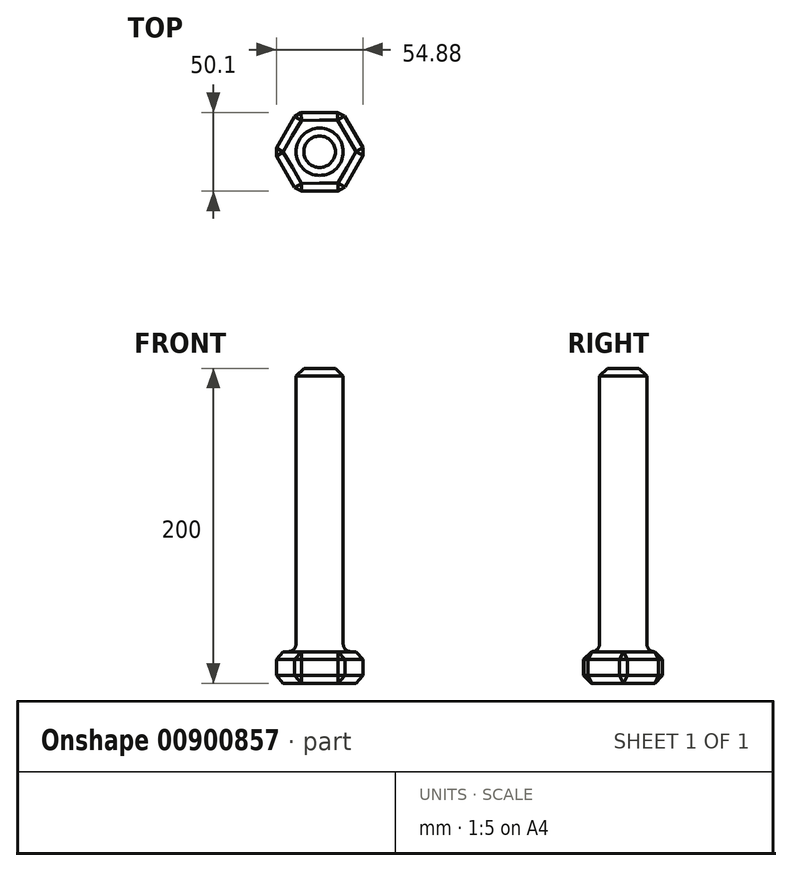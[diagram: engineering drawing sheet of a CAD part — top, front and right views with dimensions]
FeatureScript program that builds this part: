
annotation { "Feature Type Name" : "Feature", "Feature Type Description" : "" }
export const myFeature = defineFeature(function(context is Context, id is Id, definition is map)
    precondition{}
    {
        {
            var Q0;
            Q0=qCreatedBy(makeId("Top.planeOp"),FACE);
            var sketch = newSketch(context, id + "F0", { "sketchPlane" : qUnion([Q0])});
            skCircle(sketch, "E0.cCircle", {"center": v(0, 0) * mm, "radius": 25 * mm, "construction": true});
            skLineSegment(sketch, "E0.0", {"start": v(-28.87, -0.13) * mm, "end": v(-14.55, 24.94) * mm});
            skLineSegment(sketch, "E0.1", {"start": v(-14.55, 24.94) * mm, "end": v(14.32, 25.06) * mm});
            skLineSegment(sketch, "E0.2", {"start": v(14.32, 25.06) * mm, "end": v(28.87, 0.13) * mm});
            skLineSegment(sketch, "E0.3", {"start": v(28.87, 0.13) * mm, "end": v(14.55, -24.94) * mm});
            skLineSegment(sketch, "E0.4", {"start": v(14.55, -24.94) * mm, "end": v(-14.32, -25.06) * mm});
            skLineSegment(sketch, "E0.5", {"start": v(-14.32, -25.06) * mm, "end": v(-28.87, -0.13) * mm});
            skPoint(sketch, "E0.0.midPoint", {"position": v(-21.7, 12.4) * mm});
            skSolve(sketch);
        }
        {
            var Q0;
            Q0=makeQuery(id+"F0.imprint","IMPRINT",FACE,{"disambiguationData":[TD([[makeQuery(id+"F0.imprint","IMPRINT",EDGE,{"derivedFrom":sQuery(id+"F0.wireOp",EDGE,"E0.0")}),-1.0]])]});
            extrude(context, id + "F1", {"entities" : qUnion([Q0]), "depth" : 20 * mm, "offsetDistance" : 25 * mm});
        }
        {
            var Q0;
            Q0=qCreatedBy(makeId("Top.planeOp"),FACE);
            var sketch = newSketch(context, id + "F2", { "sketchPlane" : qUnion([Q0])});
            skCircle(sketch, "E1", {"center": v(0, 0) * mm, "radius": 15 * mm});
            skSolve(sketch);
        }
        {
            var Q0;
            Q0=makeQuery(id+"F2.imprint","IMPRINT",FACE,{"disambiguationData":[TD([[makeQuery(id+"F2.imprint","IMPRINT",EDGE,{"derivedFrom":sQuery(id+"F2.wireOp",EDGE,"E1")}),1.0]])]});
            extrude(context, id + "F3", {"entities" : qUnion([Q0]), "operationType" : NewBodyOperationType.ADD, "depth" : 200 * mm, "offsetDistance" : 25 * mm});
        }
        {
            var Q0;
            Q0=makeQuery(id+"F3.opExtrude","CAP_EDGE",EDGE,{"disambiguationData":[OSD([sQuery(id+"F2.wireOp",EDGE,"E1")])],"isStart":false});
            var Q1;
            Q1=makeQuery(id+"F1.opExtrude","CAP_EDGE",EDGE,{"disambiguationData":[OSD([sQuery(id+"F0.wireOp",EDGE,"E0.0")])],"isStart":false});
            var Q2;
            Q2=makeQuery(id+"F1.opExtrude","CAP_EDGE",EDGE,{"disambiguationData":[OSD([sQuery(id+"F0.wireOp",EDGE,"E0.5")])],"isStart":false});
            var Q3;
            Q3=makeQuery(id+"F1.opExtrude","CAP_EDGE",EDGE,{"disambiguationData":[OSD([sQuery(id+"F0.wireOp",EDGE,"E0.4")])],"isStart":false});
            var Q4;
            Q4=makeQuery(id+"F1.opExtrude","CAP_EDGE",EDGE,{"disambiguationData":[OSD([sQuery(id+"F0.wireOp",EDGE,"E0.3")])],"isStart":false});
            var Q5;
            Q5=makeQuery(id+"F1.opExtrude","CAP_EDGE",EDGE,{"disambiguationData":[OSD([sQuery(id+"F0.wireOp",EDGE,"E0.1")])],"isStart":false});
            var Q6;
            Q6=makeQuery(id+"F1.opExtrude","CAP_EDGE",EDGE,{"disambiguationData":[OSD([sQuery(id+"F0.wireOp",EDGE,"E0.2")])],"isStart":false});
            var Q7;
            Q7=makeQuery(id+"F1.opExtrude","CAP_EDGE",EDGE,{"disambiguationData":[OSD([sQuery(id+"F0.wireOp",EDGE,"E0.3")])],"isStart":true});
            var Q8;
            Q8=makeQuery(id+"F1.opExtrude","CAP_EDGE",EDGE,{"disambiguationData":[OSD([sQuery(id+"F0.wireOp",EDGE,"E0.2")])],"isStart":true});
            var Q9;
            Q9=makeQuery(id+"F1.opExtrude","CAP_EDGE",EDGE,{"disambiguationData":[OSD([sQuery(id+"F0.wireOp",EDGE,"E0.1")])],"isStart":true});
            var Q10;
            Q10=makeQuery(id+"F1.opExtrude","CAP_EDGE",EDGE,{"disambiguationData":[OSD([sQuery(id+"F0.wireOp",EDGE,"E0.0")])],"isStart":true});
            var Q11;
            Q11=makeQuery(id+"F1.opExtrude","CAP_EDGE",EDGE,{"disambiguationData":[OSD([sQuery(id+"F0.wireOp",EDGE,"E0.5")])],"isStart":true});
            var Q12;
            Q12=makeQuery(id+"F1.opExtrude","CAP_EDGE",EDGE,{"disambiguationData":[OSD([sQuery(id+"F0.wireOp",EDGE,"E0.4")])],"isStart":true});
            var Q13;
            Q13=makeQuery(id+"F1.opExtrude","SWEPT_EDGE",EDGE,{"disambiguationData":[OSD([sQuery(id+"F0.wireOp",EDGE,"E0.0"),sQuery(id+"F0.wireOp",EDGE,"E0.5")])]});
            var Q14;
            Q14=makeQuery(id+"F1.opExtrude","SWEPT_EDGE",EDGE,{"disambiguationData":[OSD([sQuery(id+"F0.wireOp",EDGE,"E0.4"),sQuery(id+"F0.wireOp",EDGE,"E0.5")])]});
            var Q15;
            Q15=makeQuery(id+"F1.opExtrude","SWEPT_EDGE",EDGE,{"disambiguationData":[OSD([sQuery(id+"F0.wireOp",EDGE,"E0.0"),sQuery(id+"F0.wireOp",EDGE,"E0.1")])]});
            var Q16;
            Q16=makeQuery(id+"F1.opExtrude","SWEPT_EDGE",EDGE,{"disambiguationData":[OSD([sQuery(id+"F0.wireOp",EDGE,"E0.1"),sQuery(id+"F0.wireOp",EDGE,"E0.2")])]});
            var Q17;
            Q17=makeQuery(id+"F1.opExtrude","SWEPT_EDGE",EDGE,{"disambiguationData":[OSD([sQuery(id+"F0.wireOp",EDGE,"E0.3"),sQuery(id+"F0.wireOp",EDGE,"E0.4")])]});
            var Q18;
            Q18=makeQuery(id+"F1.opExtrude","SWEPT_EDGE",EDGE,{"disambiguationData":[OSD([sQuery(id+"F0.wireOp",EDGE,"E0.2"),sQuery(id+"F0.wireOp",EDGE,"E0.3")])]});
            chamfer(context, id + "F4", {"entities" : qUnion([Q0, Q1, Q2, Q3, Q4, Q5, Q6, Q7, Q8, Q9, Q10, Q11, Q12, Q13, Q14, Q15, Q16, Q17, Q18]), "width" : 5 * mm, "tangentPropagation" : true});
        }
        {
            var Q0;
            Q0=makeQuery(id+"F3.boolean.opBoolean","INTERSECT",EDGE,{"derivedFrom":[makeQuery(id+"F1.opExtrude","CAP_FACE",FACE,{"disambiguationData":[OSD([sQuery(id+"F0.wireOp",EDGE,"E0.0"),sQuery(id+"F0.wireOp",EDGE,"E0.1"),sQuery(id+"F0.wireOp",EDGE,"E0.2"),sQuery(id+"F0.wireOp",EDGE,"E0.3"),sQuery(id+"F0.wireOp",EDGE,"E0.4"),sQuery(id+"F0.wireOp",EDGE,"E0.5")])],"isStart":false}),makeQuery(id+"F3.opExtrude","SWEPT_FACE",FACE,{"disambiguationData":[OSD([sQuery(id+"F2.wireOp",EDGE,"E1")])]})]});
            fillet(context, id + "F5", {"entities" : qUnion([Q0]), "radius" : 5 * mm, "tangentPropagation" : true, "allowEdgeOverflow" : false});
        }
    });
